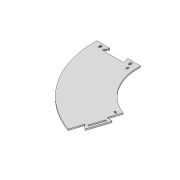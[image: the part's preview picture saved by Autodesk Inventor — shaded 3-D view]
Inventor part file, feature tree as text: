
AUTODESK INVENTOR PART (.ipt)
format: ipt  version: 2020 (Build 240168000, 168)  size: 305,152 bytes
history: native  units: mm
features: extrude x1, sketch x1
ambient origin geometry x8: Origin, YZ Plane, XZ Plane, XY Plane, X Axis, Y Axis, Z Axis, Center Point
bodies: Solid1 (feature_tree)
feature tree (2):
  extrude  "Extrusion1"  Depth=1.75mm
  sketch  "Sketch1"  dims[d0=504.787567mm d1=944.787567mm d2=50.0mm d4=360.0deg d6=7.5mm d7=7.5mm d9=68.5mm d10=7.5mm d11=7.5mm d12=3.5mm d13=3.5mm d17=50.0mm d19=360.0deg d21=4.363323mm d25=10.0mm d26=10.0mm d27=1.75mm d28=30.0mm d30=25.132741mm d32=271.25mm d33=7.5mm d34=13.5mm d36=1.75mm d40=20.0mm d44=7.0mm d45=0.0mm d46=0.0mm d47=8.0mm d48=1.75mm d50=50.0mm d52=50.0mm d54=30.0mm d62=50.0mm d64=50.0mm d66=30.0mm d67=1.75mm]
